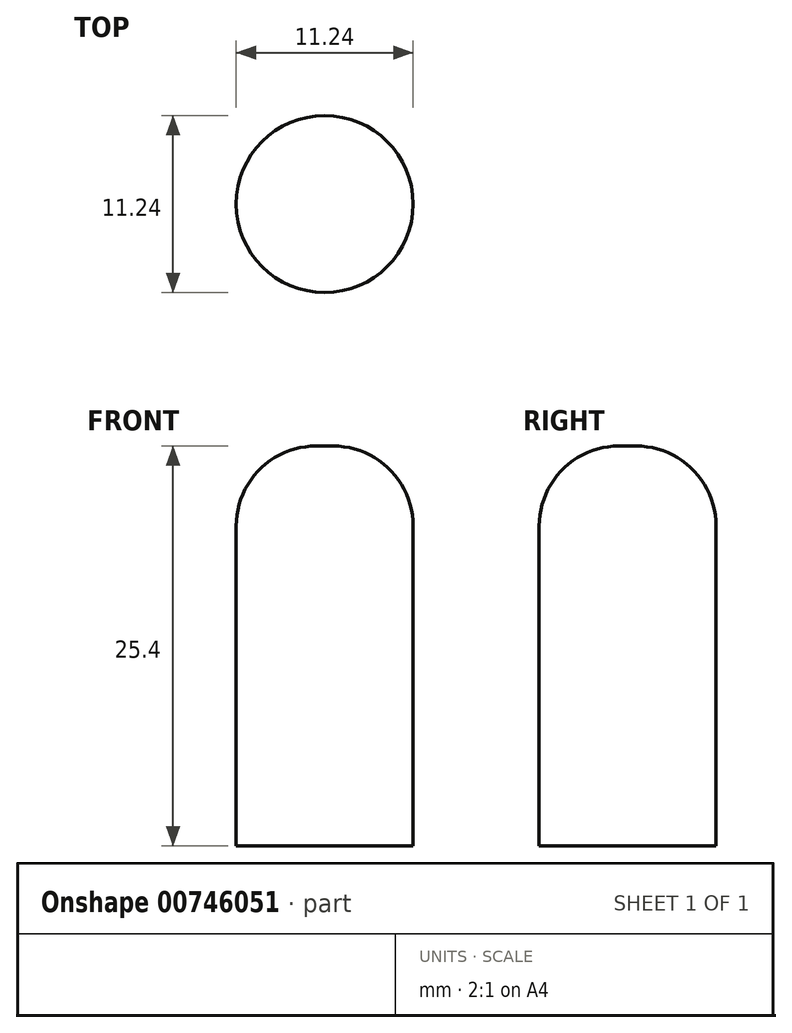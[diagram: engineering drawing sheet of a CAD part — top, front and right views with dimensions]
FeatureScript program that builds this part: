
annotation { "Feature Type Name" : "Feature", "Feature Type Description" : "" }
export const myFeature = defineFeature(function(context is Context, id is Id, definition is map)
    precondition{}
    {
        {
            var Q0;
            Q0=qCreatedBy(makeId("Top.planeOp"),FACE);
            var sketch = newSketch(context, id + "F0", { "sketchPlane" : qUnion([Q0])});
            skCircle(sketch, "E0", {"center": v(0, 0) * mm, "radius": 5.62 * mm});
            skSolve(sketch);
        }
        {
            var Q0;
            Q0 = qSketchRegion(id + "F0", true);
            extrude(context, id + "F1", {"entities" : qUnion([Q0]), "depth" : 25.4 * mm, "offsetDistance" : 25.4 * mm});
        }
        {
            var Q0;
            Q0=makeQuery(id+"F1.opExtrude","CAP_EDGE",EDGE,{"disambiguationData":[OSD([sQuery(id+"F0.wireOp",EDGE,"E0")])],"isStart":false});
            fillet(context, id + "F2", {"entities" : qUnion([Q0]), "radius" : 5.08 * mm, "tangentPropagation" : true, "allowEdgeOverflow" : false});
        }
        {
            var Q0;
            Q0=qCreatedBy(makeId("Top.planeOp"),FACE);
            var sketch = newSketch(context, id + "F3", { "sketchPlane" : qUnion([Q0])});
            skCircle(sketch, "E1", {"center": v(0, 0) * mm, "radius": 3.81 * mm});
            skSolve(sketch);
        }
        {
            var Q0;
            Q0 = qSketchRegion(id + "F3", true);
            extrude(context, id + "F4", {"entities" : qUnion([Q0]), "operationType" : NewBodyOperationType.ADD, "depth" : 3 * mm, "offsetDistance" : 25.4 * mm});
        }
    });
